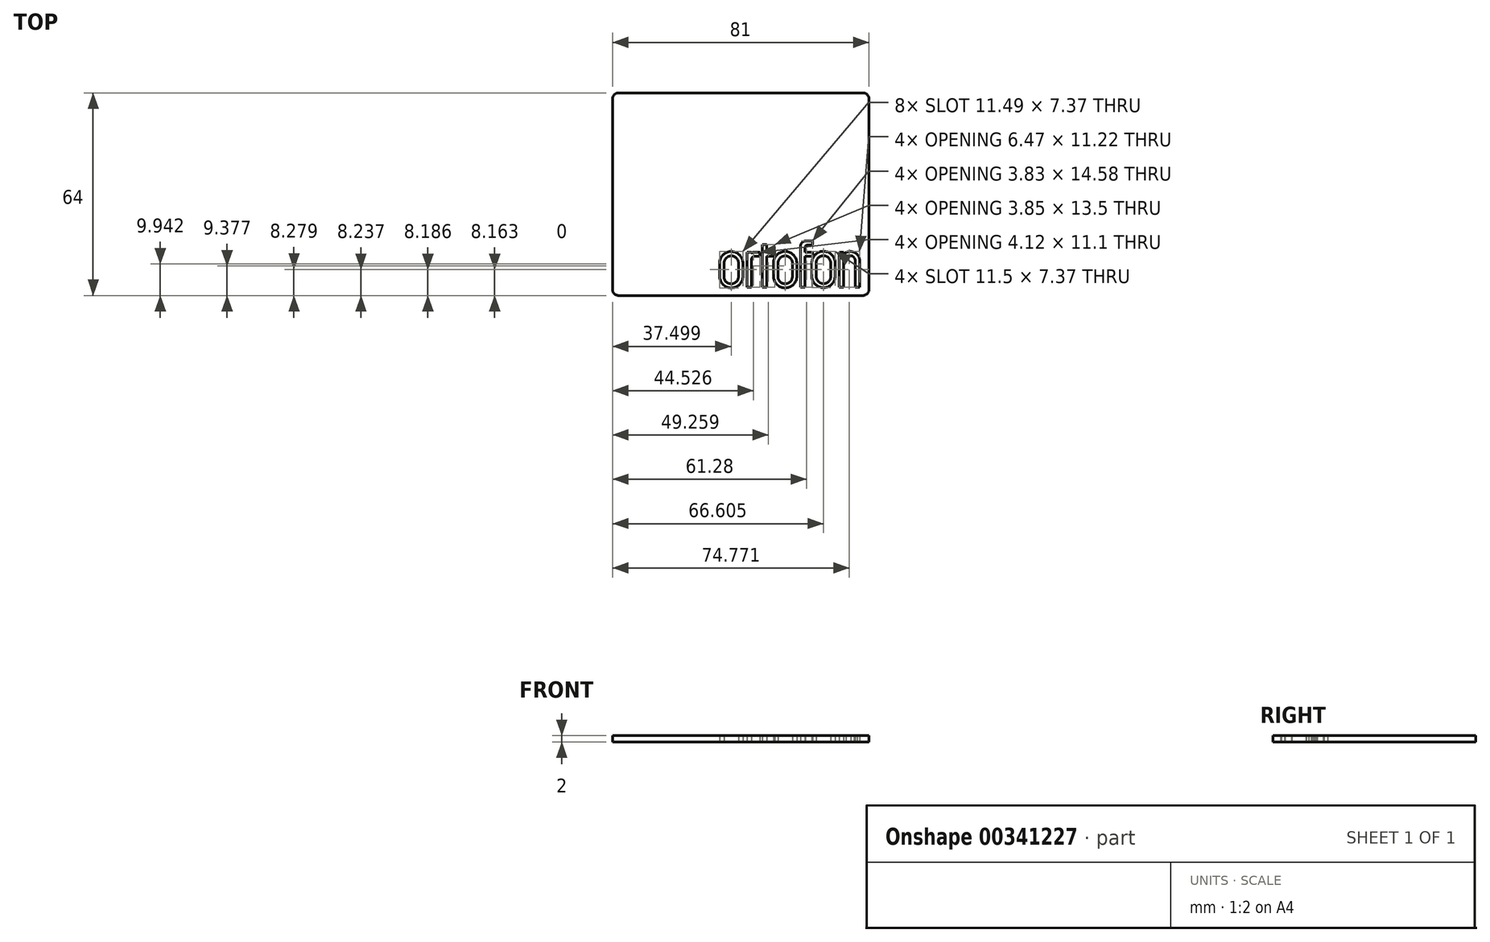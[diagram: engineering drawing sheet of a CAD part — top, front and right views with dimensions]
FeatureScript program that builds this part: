
annotation { "Feature Type Name" : "Feature", "Feature Type Description" : "" }
export const myFeature = defineFeature(function(context is Context, id is Id, definition is map)
    precondition{}
    {
        {
            var Q0;
            Q0=qCreatedBy(makeId("Top.planeOp"),FACE);
            var sketch = newSketch(context, id + "F0", { "sketchPlane" : qUnion([Q0])});
            skLineSegment(sketch, "E0.bottom", {"start": v(-38.5, 32) * mm, "end": v(38.5, 32) * mm});
            skLineSegment(sketch, "E0.top", {"start": v(-38.5, -32) * mm, "end": v(38.5, -32) * mm});
            skLineSegment(sketch, "E0.left", {"start": v(-40.5, 30) * mm, "end": v(-40.5, -30) * mm});
            skLineSegment(sketch, "E0.right", {"start": v(40.5, 30) * mm, "end": v(40.5, -30) * mm});
            skPoint(sketch, "E1.visualSharp", {"position": v(-40.5, 32) * mm});
            skArc(sketch, "E1.filletArc", {"start": v(-38.5, 32) * mm, "mid": v(-39.91, 31.41) * mm, "end": v(-40.5, 30) * mm});
            skPoint(sketch, "E2.visualSharp", {"position": v(-40.5, -32) * mm});
            skArc(sketch, "E2.filletArc", {"start": v(-40.5, -30) * mm, "mid": v(-39.91, -31.41) * mm, "end": v(-38.5, -32) * mm});
            skPoint(sketch, "E3.visualSharp", {"position": v(40.5, -32) * mm});
            skArc(sketch, "E3.filletArc", {"start": v(38.5, -32) * mm, "mid": v(39.91, -31.41) * mm, "end": v(40.5, -30) * mm});
            skPoint(sketch, "E4.visualSharp", {"position": v(40.5, 32) * mm});
            skArc(sketch, "E4.filletArc", {"start": v(40.5, 30) * mm, "mid": v(39.91, 31.41) * mm, "end": v(38.5, 32) * mm});
            skLineSegment(sketch, "E5", {"start": v(-6.68, -21.77) * mm, "end": v(-6.68, -26.17) * mm});
            skLineSegment(sketch, "E6", {"start": v(-5.28, -21.77) * mm, "end": v(-5.28, -26.17) * mm});
            skArc(sketch, "E7", {"start": v(-0.71, -21.63) * mm, "mid": v(-3.07, -19.49) * mm, "end": v(-5.28, -21.77) * mm});
            skArc(sketch, "E8.0", {"start": v(0.68, -21.5) * mm, "mid": v(-3.13, -18.09) * mm, "end": v(-6.68, -21.77) * mm});
            skLineSegment(sketch, "E9", {"start": v(-0.71, -21.63) * mm, "end": v(-0.71, -26.03) * mm});
            skLineSegment(sketch, "E10", {"start": v(0.68, -21.5) * mm, "end": v(0.68, -25.9) * mm});
            skArc(sketch, "E11.0", {"start": v(-6.68, -26.17) * mm, "mid": v(-2.87, -29.58) * mm, "end": v(0.68, -25.9) * mm});
            skPoint(sketch, "E12.orphan", {"position": v(-6.68, -26.57) * mm});
            skPoint(sketch, "E13.orphan", {"position": v(-5.28, -26.57) * mm});
            skPoint(sketch, "E14.orphan", {"position": v(0.68, -26.57) * mm});
            skPoint(sketch, "E15.orphan", {"position": v(-0.71, -26.57) * mm});
            skArc(sketch, "E16", {"start": v(-5.28, -26.17) * mm, "mid": v(-2.93, -28.31) * mm, "end": v(-0.71, -26.03) * mm});
            skLineSegment(sketch, "E17", {"start": v(10.34, -21.77) * mm, "end": v(10.34, -26.16) * mm});
            skLineSegment(sketch, "E18", {"start": v(11.74, -21.77) * mm, "end": v(11.74, -26.16) * mm});
            skArc(sketch, "E19", {"start": v(16.31, -21.62) * mm, "mid": v(13.96, -19.48) * mm, "end": v(11.74, -21.77) * mm});
            skArc(sketch, "E20.0", {"start": v(17.7, -21.5) * mm, "mid": v(13.9, -18.08) * mm, "end": v(10.34, -21.77) * mm});
            skLineSegment(sketch, "E21", {"start": v(16.31, -21.62) * mm, "end": v(16.31, -26.02) * mm});
            skLineSegment(sketch, "E22", {"start": v(17.7, -21.5) * mm, "end": v(17.7, -25.89) * mm});
            skArc(sketch, "E23.0", {"start": v(10.34, -26.16) * mm, "mid": v(14.15, -29.58) * mm, "end": v(17.7, -25.89) * mm});
            skArc(sketch, "E24", {"start": v(11.74, -26.16) * mm, "mid": v(14.1, -28.3) * mm, "end": v(16.31, -26.02) * mm});
            skLineSegment(sketch, "E25", {"start": v(22.42, -21.7) * mm, "end": v(22.42, -26.1) * mm});
            skLineSegment(sketch, "E26", {"start": v(23.82, -21.7) * mm, "end": v(23.82, -26.1) * mm});
            skArc(sketch, "E27", {"start": v(28.4, -21.56) * mm, "mid": v(26.04, -19.41) * mm, "end": v(23.82, -21.7) * mm});
            skArc(sketch, "E28.0", {"start": v(29.79, -21.43) * mm, "mid": v(25.97, -18.02) * mm, "end": v(22.42, -21.7) * mm});
            skLineSegment(sketch, "E29", {"start": v(28.4, -21.56) * mm, "end": v(28.4, -25.95) * mm});
            skLineSegment(sketch, "E30", {"start": v(29.79, -21.43) * mm, "end": v(29.79, -25.83) * mm});
            skArc(sketch, "E31.0", {"start": v(22.42, -26.1) * mm, "mid": v(26.24, -29.51) * mm, "end": v(29.79, -25.83) * mm});
            skArc(sketch, "E32", {"start": v(23.82, -26.1) * mm, "mid": v(26.18, -28.24) * mm, "end": v(28.4, -25.95) * mm});
            skLineSegment(sketch, "E33", {"start": v(1.97, -18.26) * mm, "end": v(1.97, -29.36) * mm});
            skLineSegment(sketch, "E34", {"start": v(1.97, -29.36) * mm, "end": v(3.37, -29.36) * mm});
            skLineSegment(sketch, "E35", {"start": v(3.37, -29.36) * mm, "end": v(3.37, -20.61) * mm});
            skLineSegment(sketch, "E36", {"start": v(1.97, -18.26) * mm, "end": v(3.37, -18.26) * mm});
            skLineSegment(sketch, "E37", {"start": v(3.37, -18.26) * mm, "end": v(3.37, -18.67) * mm});
            skLineSegment(sketch, "E38", {"start": v(6.08, -18.26) * mm, "end": v(6.08, -19.61) * mm});
            skLineSegment(sketch, "E39", {"start": v(6.08, -19.61) * mm, "end": v(4.37, -19.61) * mm});
            skLineSegment(sketch, "E40", {"start": v(6.08, -18.26) * mm, "end": v(4.23, -18.26) * mm});
            skPoint(sketch, "E41.visualSharp", {"position": v(3.37, -19.61) * mm});
            skArc(sketch, "E41.filletArc", {"start": v(4.37, -19.61) * mm, "mid": v(3.66, -19.9) * mm, "end": v(3.37, -20.61) * mm});
            skArc(sketch, "E42", {"start": v(4.23, -18.26) * mm, "mid": v(3.75, -18.37) * mm, "end": v(3.37, -18.67) * mm});
            skLineSegment(sketch, "E43", {"start": v(6.83, -15.87) * mm, "end": v(6.83, -29.37) * mm});
            skLineSegment(sketch, "E44", {"start": v(6.83, -29.37) * mm, "end": v(8.23, -29.37) * mm});
            skLineSegment(sketch, "E45", {"start": v(8.23, -29.37) * mm, "end": v(8.23, -19.62) * mm});
            skLineSegment(sketch, "E46", {"start": v(6.83, -15.87) * mm, "end": v(8.23, -15.87) * mm});
            skLineSegment(sketch, "E47", {"start": v(8.23, -15.87) * mm, "end": v(8.23, -18.27) * mm});
            skLineSegment(sketch, "E48", {"start": v(10.68, -18.27) * mm, "end": v(10.68, -19.62) * mm});
            skLineSegment(sketch, "E49", {"start": v(10.68, -19.62) * mm, "end": v(8.23, -19.62) * mm});
            skLineSegment(sketch, "E50", {"start": v(10.68, -18.27) * mm, "end": v(8.23, -18.27) * mm});
            skLineSegment(sketch, "E51", {"start": v(18.86, -16.2) * mm, "end": v(18.86, -29.35) * mm});
            skLineSegment(sketch, "E52", {"start": v(18.86, -29.35) * mm, "end": v(20.26, -29.35) * mm});
            skLineSegment(sketch, "E53", {"start": v(20.26, -29.35) * mm, "end": v(20.26, -19.6) * mm});
            skLineSegment(sketch, "E54", {"start": v(22.69, -14.77) * mm, "end": v(22.69, -15.97) * mm});
            skLineSegment(sketch, "E55", {"start": v(22.69, -15.97) * mm, "end": v(21.26, -15.97) * mm});
            skLineSegment(sketch, "E56", {"start": v(22.69, -14.77) * mm, "end": v(20.4, -14.77) * mm});
            skArc(sketch, "E57.filletArc", {"start": v(21.26, -15.97) * mm, "mid": v(20.56, -16.26) * mm, "end": v(20.26, -16.97) * mm});
            skArc(sketch, "E58", {"start": v(20.4, -14.77) * mm, "mid": v(19.4, -15.23) * mm, "end": v(18.86, -16.2) * mm});
            skLineSegment(sketch, "E59", {"start": v(20.26, -18.28) * mm, "end": v(22.7, -18.28) * mm});
            skLineSegment(sketch, "E60", {"start": v(22.7, -18.28) * mm, "end": v(22.7, -19.6) * mm});
            skLineSegment(sketch, "E61", {"start": v(22.7, -19.6) * mm, "end": v(20.26, -19.6) * mm});
            skLineSegment(sketch, "E62.trimOffspring", {"start": v(20.26, -18.28) * mm, "end": v(20.26, -16.97) * mm});
            skLineSegment(sketch, "E63", {"start": v(31.04, -18.28) * mm, "end": v(31.04, -29.33) * mm});
            skLineSegment(sketch, "E64", {"start": v(31.04, -29.33) * mm, "end": v(32.44, -29.33) * mm});
            skLineSegment(sketch, "E65", {"start": v(32.44, -29.33) * mm, "end": v(32.44, -21.26) * mm});
            skArc(sketch, "E66", {"start": v(33.18, -19.9) * mm, "mid": v(32.64, -20.48) * mm, "end": v(32.44, -21.26) * mm});
            skArc(sketch, "E67", {"start": v(34.7, -19.42) * mm, "mid": v(33.9, -19.51) * mm, "end": v(33.18, -19.9) * mm});
            skArc(sketch, "E68", {"start": v(35.7, -19.9) * mm, "mid": v(35.26, -19.55) * mm, "end": v(34.7, -19.42) * mm});
            skArc(sketch, "E69", {"start": v(36.1, -20.67) * mm, "mid": v(35.94, -20.27) * mm, "end": v(35.7, -19.9) * mm});
            skLineSegment(sketch, "E70", {"start": v(36.1, -20.67) * mm, "end": v(36.1, -29.33) * mm});
            skLineSegment(sketch, "E71", {"start": v(36.1, -29.33) * mm, "end": v(37.5, -29.33) * mm});
            skLineSegment(sketch, "E72", {"start": v(37.5, -29.33) * mm, "end": v(37.5, -20.94) * mm});
            skLineSegment(sketch, "E73", {"start": v(31.04, -18.28) * mm, "end": v(32.43, -18.28) * mm});
            skLineSegment(sketch, "E74", {"start": v(32.43, -18.28) * mm, "end": v(32.43, -18.77) * mm});
            skArc(sketch, "E75", {"start": v(34.72, -18.1) * mm, "mid": v(33.53, -18.29) * mm, "end": v(32.43, -18.77) * mm});
            skArc(sketch, "E76", {"start": v(36.75, -18.96) * mm, "mid": v(35.82, -18.33) * mm, "end": v(34.72, -18.1) * mm});
            skArc(sketch, "E77", {"start": v(37.5, -20.94) * mm, "mid": v(37.31, -19.88) * mm, "end": v(36.75, -18.96) * mm});
            skSolve(sketch);
        }
        {
            var Q0;
            Q0 = qSketchRegion(id + "F0", true);
            var Q1;
            Q1=makeQuery(id+"F0.imprint","IMPRINT",FACE,{"disambiguationData":[TD([[makeQuery(id+"F0.imprint","IMPRINT",EDGE,{"derivedFrom":sQuery(id+"F0.wireOp",EDGE,"E6")}),1.0]])]});
            var Q2;
            Q2=makeQuery(id+"F0.imprint","IMPRINT",FACE,{"disambiguationData":[TD([[makeQuery(id+"F0.imprint","IMPRINT",EDGE,{"derivedFrom":sQuery(id+"F0.wireOp",EDGE,"E18")}),1.0]])]});
            var Q3;
            Q3=makeQuery(id+"F0.imprint","IMPRINT",FACE,{"disambiguationData":[TD([[makeQuery(id+"F0.imprint","IMPRINT",EDGE,{"derivedFrom":sQuery(id+"F0.wireOp",EDGE,"E26")}),1.0]])]});
            extrude(context, id + "F1", {"entities" : qUnion([Q0, Q1, Q2, Q3]), "depth" : 2 * mm});
        }
    });
